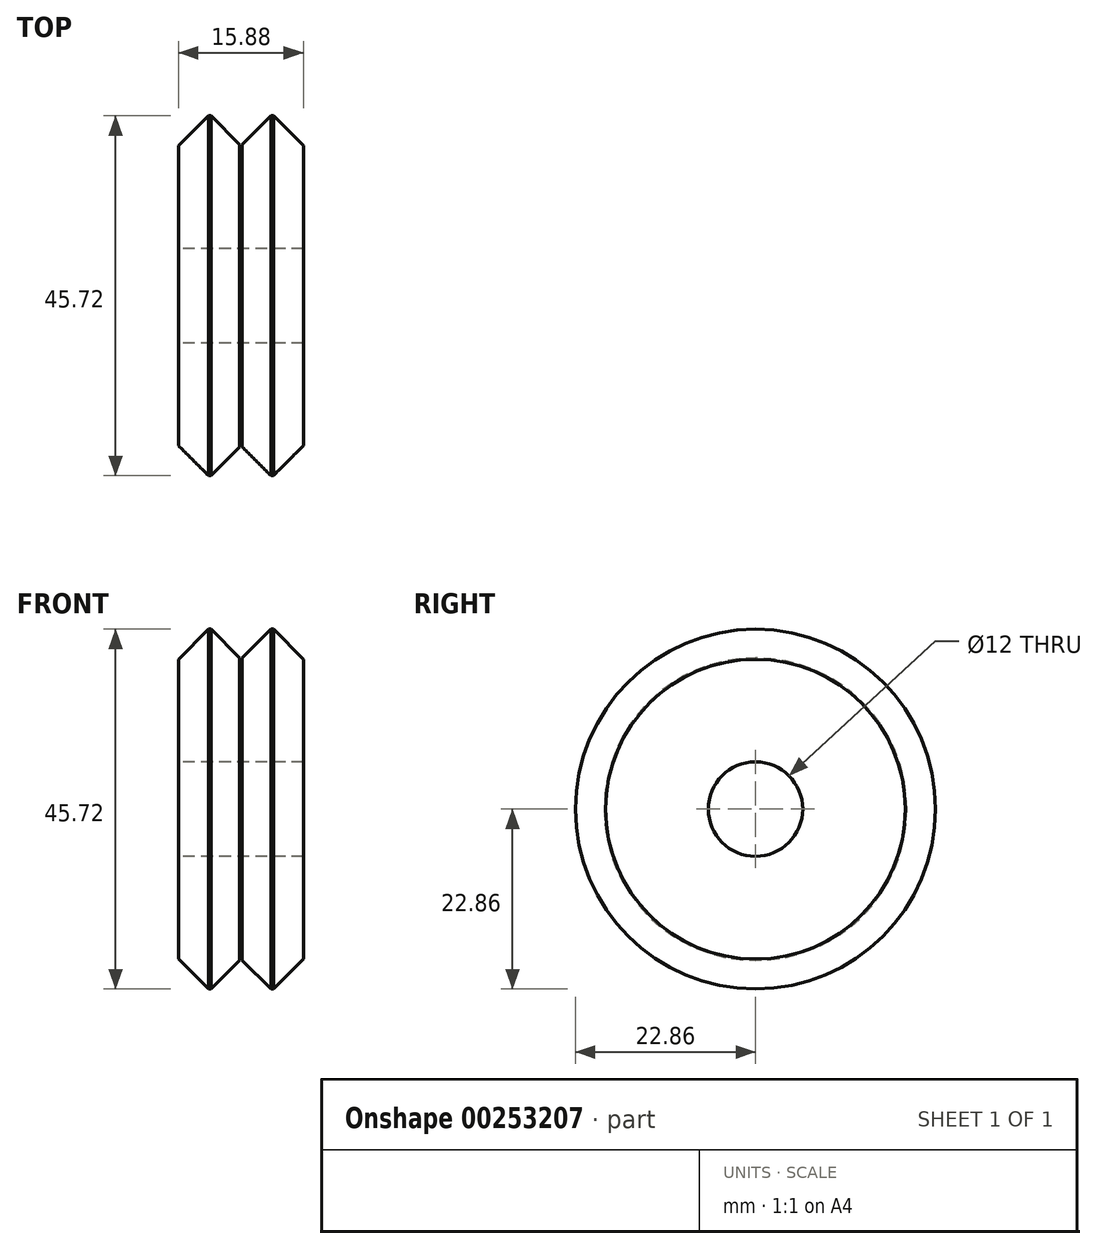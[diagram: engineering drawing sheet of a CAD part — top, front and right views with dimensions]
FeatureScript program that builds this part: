
annotation { "Feature Type Name" : "Feature", "Feature Type Description" : "" }
export const myFeature = defineFeature(function(context is Context, id is Id, definition is map)
    precondition{}
    {
        {
            var Q0;
            Q0=qCreatedBy(makeId("Right.planeOp"),FACE);
            var sketch = newSketch(context, id + "F0", { "sketchPlane" : qUnion([Q0])});
            skCircle(sketch, "E0", {"center": v(0, 0) * mm, "radius": 22.86 * mm});
            skCircle(sketch, "E1", {"center": v(0, 0) * mm, "radius": 6 * mm});
            skSolve(sketch);
        }
        {
            var Q0;
            Q0 = qSketchRegion(id + "F0", true);
            extrude(context, id + "F1", {"entities" : qUnion([Q0]), "endBound" : BoundingType.SYMMETRIC, "depth" : 15.88 * mm});
        }
        {
            var Q0;
            Q0=qCreatedBy(makeId("Top.planeOp"),FACE);
            var sketch = newSketch(context, id + "F2", { "sketchPlane" : qUnion([Q0])});
            skPoint(sketch, "E2", {"position": v(-7.94, -22.86) * mm});
            skPoint(sketch, "E3", {"position": v(7.94, -22.86) * mm});
            skPoint(sketch, "E4", {"position": v(0, 0) * mm});
            skLineSegment(sketch, "E5", {"start": v(15.64, 0) * mm, "end": v(15.64, -19.05) * mm, "construction": true});
            skLineSegment(sketch, "E6", {"start": v(12.46, 0) * mm, "end": v(12.46, -26.97) * mm, "construction": true});
            skLineSegment(sketch, "E7", {"start": v(12.46, -26.97) * mm, "end": v(0, -26.97) * mm, "construction": true});
            skLineSegment(sketch, "E8", {"start": v(15.64, -19.05) * mm, "end": v(-23.85, -19.05) * mm, "construction": true});
            skLineSegment(sketch, "E9", {"start": v(-19.8, -7.18) * mm, "end": v(31.32, -58.3) * mm, "construction": true});
            skLineSegment(sketch, "E10", {"start": v(0, -26.97) * mm, "end": v(0, -41.28) * mm, "construction": true});
            skLineSegment(sketch, "E11.MirrorCS", {"start": v(19.8, -7.18) * mm, "end": v(-31.32, -58.3) * mm, "construction": true});
            skPoint(sketch, "E12.orphan", {"position": v(0, -19.05) * mm});
            skLineSegment(sketch, "E13", {"start": v(23.19, -22.86) * mm, "end": v(-20.17, -22.86) * mm, "construction": true});
            skLineSegment(sketch, "E14", {"start": v(-7.94, -47.19) * mm, "end": v(-7.94, -2.65) * mm, "construction": true});
            skLineSegment(sketch, "E15.MirrorCS", {"start": v(7.94, -47.19) * mm, "end": v(7.94, -2.65) * mm, "construction": true});
            skLineSegment(sketch, "E16", {"start": v(-7.94, -19.04) * mm, "end": v(-4.11, -22.86) * mm});
            skLineSegment(sketch, "E17", {"start": v(-4.11, -22.86) * mm, "end": v(-3.8, -22.86) * mm});
            skLineSegment(sketch, "E18", {"start": v(-7.94, -19.04) * mm, "end": v(-7.94, -22.86) * mm});
            skLineSegment(sketch, "E19", {"start": v(-4.11, -22.86) * mm, "end": v(-7.94, -22.86) * mm});
            skLineSegment(sketch, "E20", {"start": v(-7.94, -19.04) * mm, "end": v(0.2, -19.04) * mm, "construction": true});
            skLineSegment(sketch, "E21", {"start": v(0, -19.05) * mm, "end": v(0, -19) * mm, "construction": true});
            skLineSegment(sketch, "E22", {"start": v(-0.02, -19.01) * mm, "end": v(0.02, -19.01) * mm});
            skPoint(sketch, "E23.orphan", {"position": v(-0.02, -19.05) * mm});
            skPoint(sketch, "E24.orphan", {"position": v(0.02, -19.05) * mm});
            skLineSegment(sketch, "E25", {"start": v(-0.15, -19.2) * mm, "end": v(-3.8, -22.86) * mm});
            skLineSegment(sketch, "E26", {"start": v(-3.8, -22.86) * mm, "end": v(3.8, -22.86) * mm});
            skLineSegment(sketch, "E27", {"start": v(3.8, -22.86) * mm, "end": v(0.15, -19.2) * mm});
            skLineSegment(sketch, "E28", {"start": v(3.8, -22.86) * mm, "end": v(4.11, -22.86) * mm});
            skLineSegment(sketch, "E29", {"start": v(4.11, -22.86) * mm, "end": v(7.94, -19.04) * mm});
            skLineSegment(sketch, "E30", {"start": v(7.94, -19.04) * mm, "end": v(7.94, -22.86) * mm});
            skLineSegment(sketch, "E31", {"start": v(7.94, -22.86) * mm, "end": v(4.11, -22.86) * mm});
            skLineSegment(sketch, "E32.0", {"start": v(0.15, -19.2) * mm, "end": v(0.15, -19.01) * mm});
            skLineSegment(sketch, "E33", {"start": v(0.02, -19.01) * mm, "end": v(0.15, -19.01) * mm});
            skLineSegment(sketch, "E34.MirrorCS", {"start": v(-0.02, -19.01) * mm, "end": v(-0.15, -19.01) * mm});
            skLineSegment(sketch, "E35.MirrorCS", {"start": v(-0.15, -19.2) * mm, "end": v(-0.15, -19.01) * mm});
            skSolve(sketch);
        }
        {
            var Q0;
            Q0=makeQuery(id+"F2.imprint","IMPRINT",FACE,{"disambiguationData":[TD([[makeQuery(id+"F2.imprint","IMPRINT",EDGE,{"derivedFrom":sQuery(id+"F2.wireOp",EDGE,"E16")}),-1.0]])]});
            var Q1;
            Q1=makeQuery(id+"F2.imprint","IMPRINT",FACE,{"disambiguationData":[TD([[makeQuery(id+"F2.imprint","IMPRINT",EDGE,{"derivedFrom":sQuery(id+"F2.wireOp",EDGE,"E22")}),-1.0]])]});
            var Q2;
            Q2=makeQuery(id+"F2.imprint","IMPRINT",FACE,{"disambiguationData":[TD([[makeQuery(id+"F2.imprint","IMPRINT",EDGE,{"derivedFrom":sQuery(id+"F2.wireOp",EDGE,"E29")}),-1.0]])]});
            var Q3;
            Q3=makeQuery(id+"F1.opExtrude","CAP_EDGE",EDGE,{"disambiguationData":[OSD([sQuery(id+"F0.wireOp",EDGE,"E0")])],"isStart":false});
            sweep(context, id + "F3", {"operationType" : NewBodyOperationType.REMOVE, "profiles" : qUnion([Q0, Q1, Q2]), "path" : qUnion([Q3])});
        }
    });
